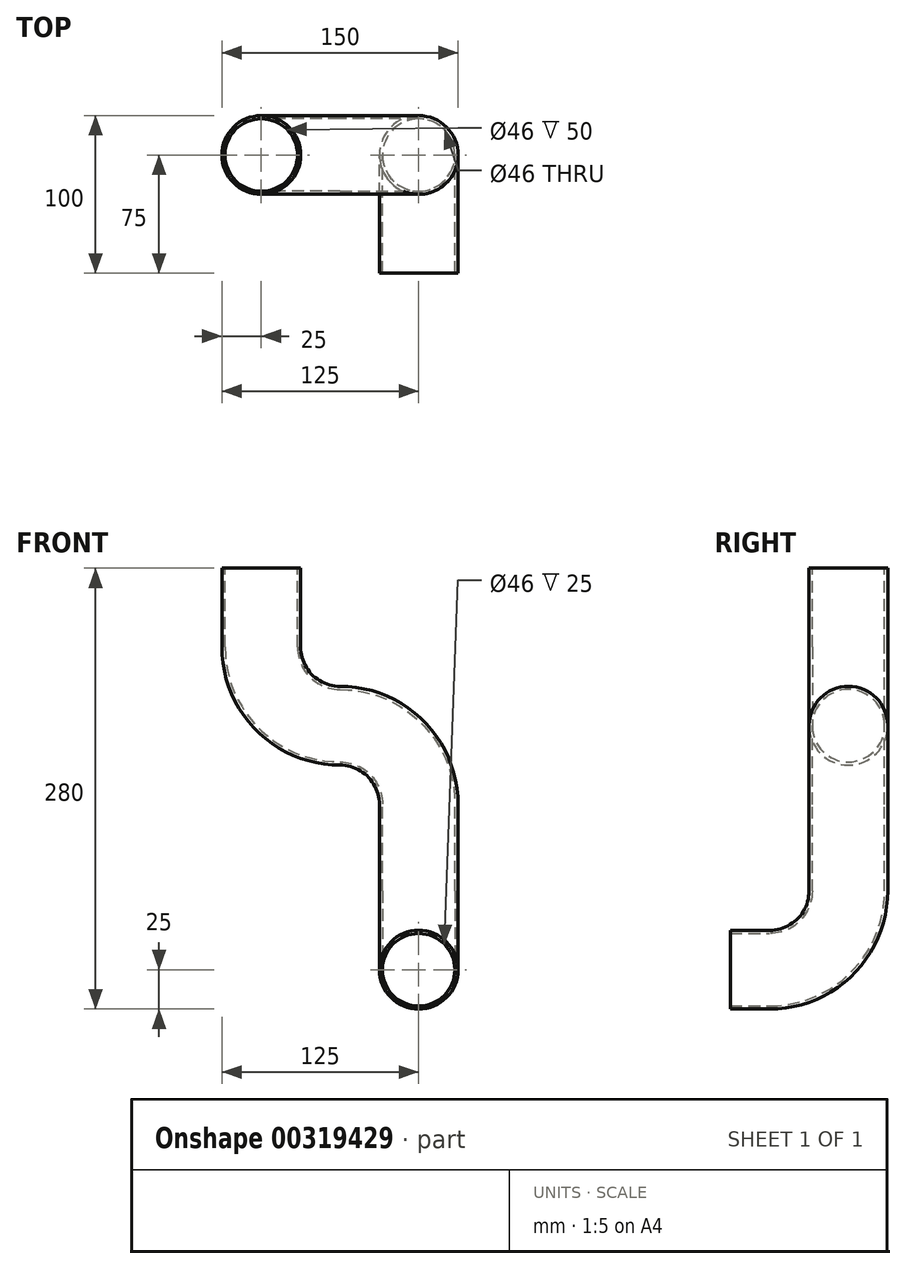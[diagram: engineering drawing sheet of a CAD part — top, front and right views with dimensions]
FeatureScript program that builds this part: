
annotation { "Feature Type Name" : "Feature", "Feature Type Description" : "" }
export const myFeature = defineFeature(function(context is Context, id is Id, definition is map)
    precondition{}
    {
        {
            var Q0;
            Q0=qCreatedBy(makeId("Front.planeOp"),FACE);
            var sketch = newSketch(context, id + "F0", { "sketchPlane" : qUnion([Q0])});
            skCircle(sketch, "E0", {"center": v(0, 0) * mm, "radius": 25 * mm});
            skCircle(sketch, "E1", {"center": v(0, 0) * mm, "radius": 23 * mm});
            skSolve(sketch);
        }
        {
            var Q0;
            Q0=qCreatedBy(makeId("Right.planeOp"),FACE);
            var sketch = newSketch(context, id + "F1", { "sketchPlane" : qUnion([Q0])});
            skLineSegment(sketch, "E2", {"start": v(75, 105) * mm, "end": v(75, 50) * mm});
            skLineSegment(sketch, "E3", {"start": v(0, 0) * mm, "end": v(25, 0) * mm});
            skArc(sketch, "E4", {"start": v(25, 0) * mm, "mid": v(60.36, 14.64) * mm, "end": v(75, 50) * mm});
            skSolve(sketch);
        }
        {
            var Q0;
            Q0=qCreatedBy(makeId("Front.planeOp"),FACE);
            var Q1;
            Q1=sQuery(id+"F1.wireOp",VERTEX,"E4.end");
            cPlane(context, id + "F2", {"entities" : qUnion([Q0, Q1]), "cplaneType" : CPlaneType.PLANE_POINT, "offset" : 25 * mm, "width" : 150 * mm, "height" : 150 * mm});
        }
        {
            var Q0;
            Q0=qCreatedBy(id+"F2.planeOp",FACE);
            var sketch = newSketch(context, id + "F3", { "sketchPlane" : qUnion([Q0])});
            skLineSegment(sketch, "E5", {"start": v(-50, 155) * mm, "end": v(-50, 155) * mm});
            skArc(sketch, "E6", {"start": v(-50, 155) * mm, "mid": v(-14.64, 140.36) * mm, "end": v(0, 105) * mm});
            skArc(sketch, "E7", {"start": v(-100, 205) * mm, "mid": v(-85.36, 169.64) * mm, "end": v(-50, 155) * mm});
            skLineSegment(sketch, "E8", {"start": v(-100, 255) * mm, "end": v(-100, 205) * mm});
            skSolve(sketch);
        }
        {
            var Q0;
            Q0 = qSketchRegion(id + "F0", true);
            var Q1;
            Q1=sQuery(id+"F1.wireOp",EDGE,"E4");
            var Q2;
            Q2=sQuery(id+"F1.wireOp",EDGE,"E3");
            var Q3;
            Q3=sQuery(id+"F1.wireOp",EDGE,"E2");
            var Q4;
            Q4=sQuery(id+"F3.wireOp",EDGE,"E6");
            var Q5;
            Q5=sQuery(id+"F3.wireOp",EDGE,"E5");
            var Q6;
            Q6=sQuery(id+"F3.wireOp",EDGE,"E7");
            var Q7;
            Q7=sQuery(id+"F3.wireOp",EDGE,"E8");
            sweep(context, id + "F4", {"profiles" : qUnion([Q0]), "path" : qUnion([Q1, Q2, Q3, Q4, Q5, Q6, Q7])});
        }
    });
